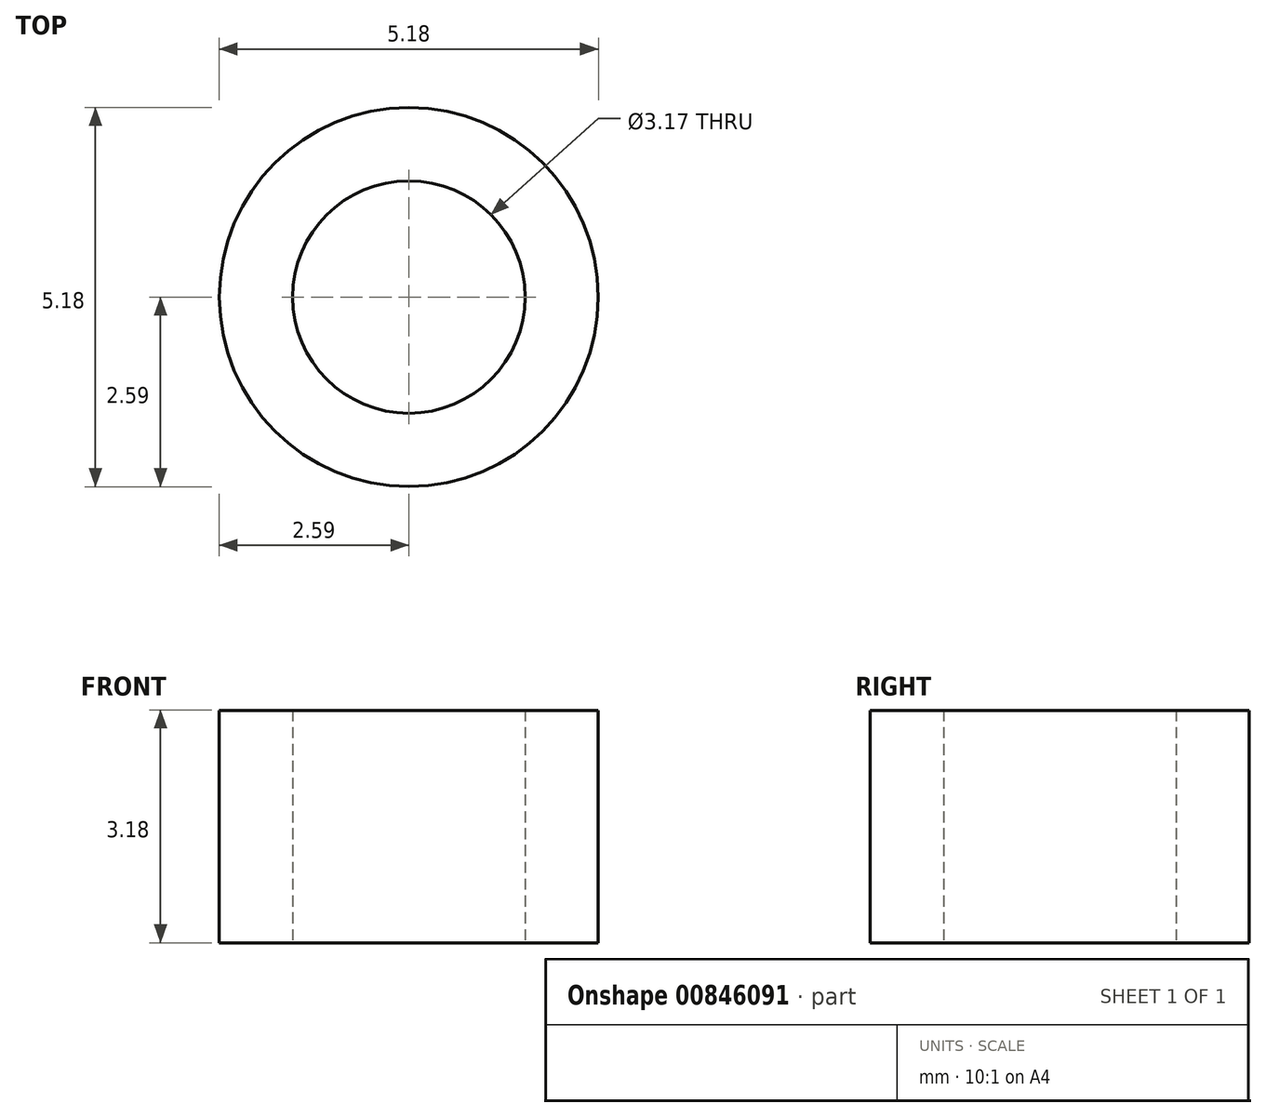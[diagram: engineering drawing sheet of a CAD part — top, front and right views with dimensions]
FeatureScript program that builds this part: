
annotation { "Feature Type Name" : "Feature", "Feature Type Description" : "" }
export const myFeature = defineFeature(function(context is Context, id is Id, definition is map)
    precondition{}
    {
        {
            var Q0;
            Q0=qCreatedBy(makeId("Top.planeOp"),FACE);
            var sketch = newSketch(context, id + "F0", { "sketchPlane" : qUnion([Q0])});
            skCircle(sketch, "E0", {"center": v(0, 0) * mm, "radius": 1.59 * mm});
            skCircle(sketch, "E1", {"center": v(0, 0) * mm, "radius": 2.59 * mm});
            skSolve(sketch);
        }
        {
            var Q0;
            Q0=makeQuery(id+"F0.imprint","IMPRINT",FACE,{"disambiguationData":[TD([[makeQuery(id+"F0.imprint","IMPRINT",EDGE,{"derivedFrom":sQuery(id+"F0.wireOp",EDGE,"E0")}),-1.0]])]});
            extrude(context, id + "F1", {"entities" : qUnion([Q0]), "depth" : 3.17 * mm, "offsetDistance" : 25.4 * mm});
        }
    });
